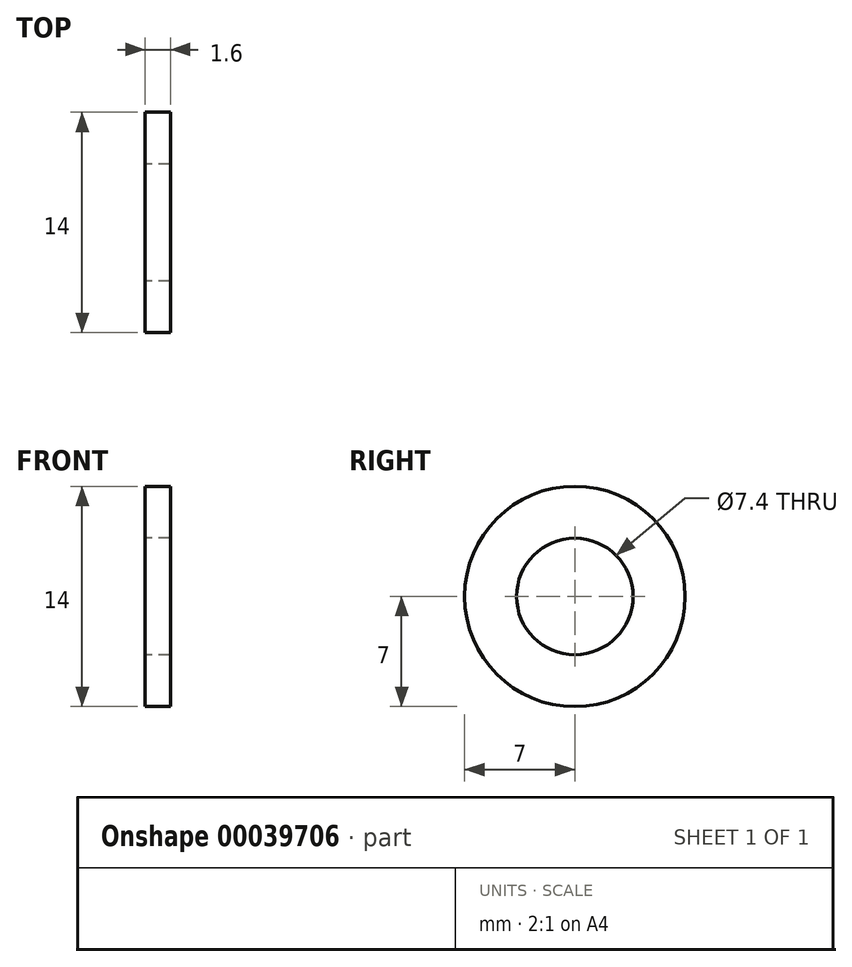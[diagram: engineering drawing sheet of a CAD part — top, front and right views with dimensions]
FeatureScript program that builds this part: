
annotation { "Feature Type Name" : "Feature", "Feature Type Description" : "" }
export const myFeature = defineFeature(function(context is Context, id is Id, definition is map)
    precondition{}
    {
        {
            var Q0;
            Q0=qCreatedBy(makeId("Right.planeOp"),FACE);
            var sketch = newSketch(context, id + "F0", { "sketchPlane" : qUnion([Q0])});
            skCircle(sketch, "E0", {"center": v(0, 0) * mm, "radius": 7 * mm});
            skCircle(sketch, "E1", {"center": v(0, 0) * mm, "radius": 3.7 * mm});
            skSolve(sketch);
        }
        {
            var Q0;
            Q0=makeQuery(id+"F0.imprint","IMPRINT",FACE,{"disambiguationData":[TD([[makeQuery(id+"F0.imprint","IMPRINT",EDGE,{"derivedFrom":sQuery(id+"F0.wireOp",EDGE,"E0")}),1.0]])]});
            extrude(context, id + "F1", {"entities" : qUnion([Q0]), "depth" : 1.6 * mm});
        }
    });
